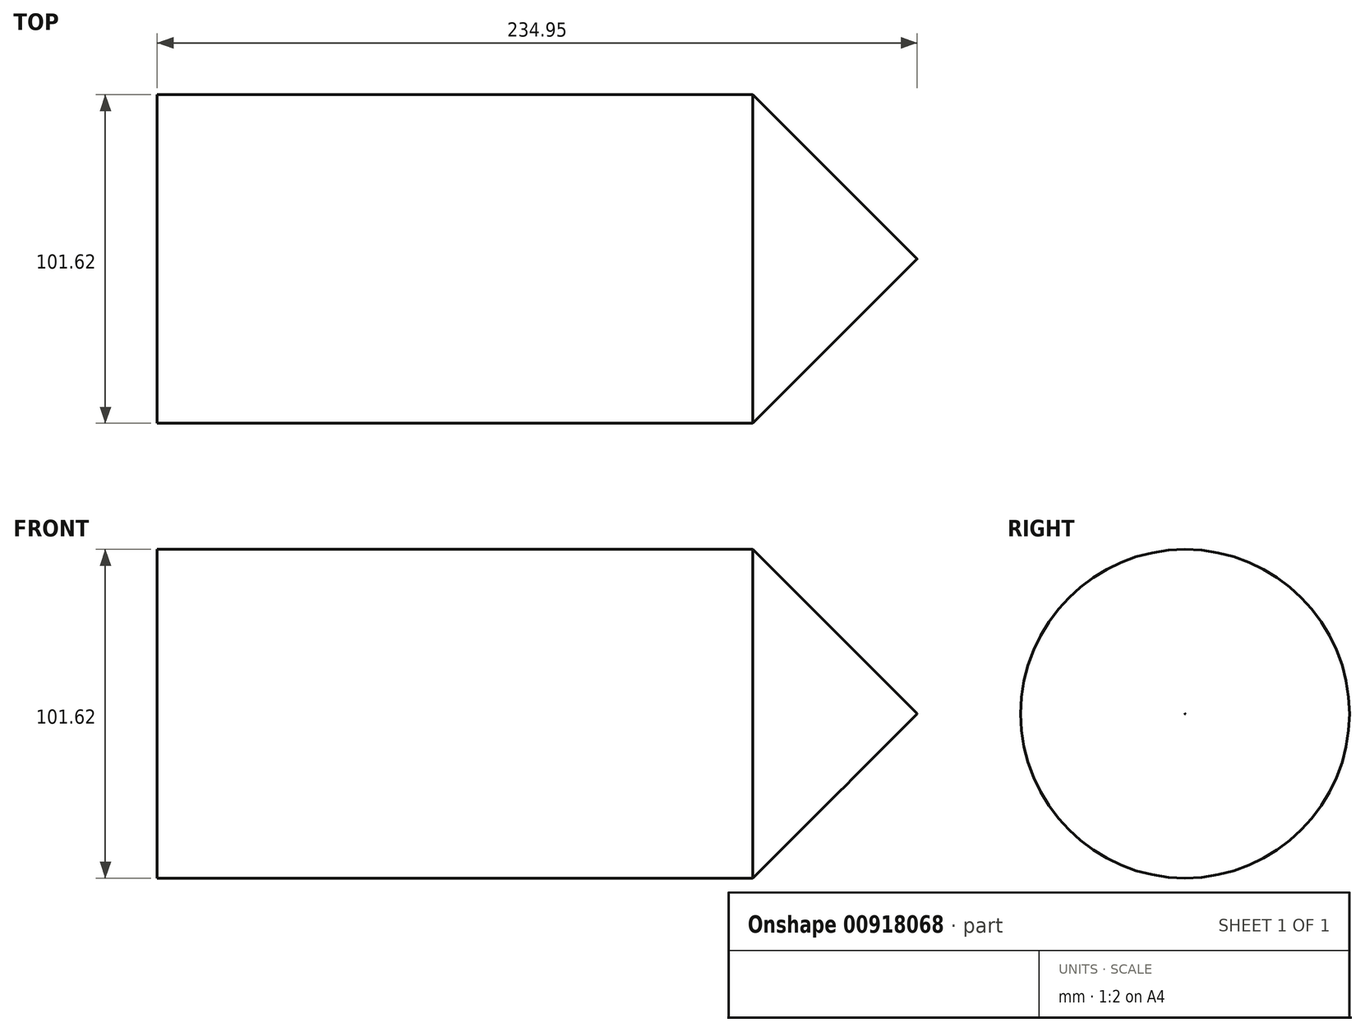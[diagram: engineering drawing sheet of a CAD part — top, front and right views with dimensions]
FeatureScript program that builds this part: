
annotation { "Feature Type Name" : "Feature", "Feature Type Description" : "" }
export const myFeature = defineFeature(function(context is Context, id is Id, definition is map)
    precondition{}
    {
        {
            var Q0;
            Q0=qCreatedBy(makeId("Right.planeOp"),FACE);
            var sketch = newSketch(context, id + "F0", { "sketchPlane" : qUnion([Q0])});
            skCircle(sketch, "E0", {"center": v(0, 0) * mm, "radius": 50.81 * mm});
            skSolve(sketch);
        }
        {
            var Q0;
            Q0=makeQuery(id+"F0.imprint","IMPRINT",FACE,{"disambiguationData":[TD([[makeQuery(id+"F0.imprint","IMPRINT",EDGE,{"derivedFrom":sQuery(id+"F0.wireOp",EDGE,"E0")}),1.0]])]});
            extrude(context, id + "F1", {"entities" : qUnion([Q0]), "depth" : 82.55 * mm, "offsetDistance" : 25.4 * mm});
        }
        {
            var Q0;
            Q0=makeQuery(id+"F1.opExtrude","CAP_EDGE",EDGE,{"disambiguationData":[OSD([sQuery(id+"F0.wireOp",EDGE,"E0")])],"isStart":false});
            chamfer(context, id + "F2", {"entities" : qUnion([Q0]), "width" : 50.8 * mm, "tangentPropagation" : true});
        }
        {
            var Q0;
            Q0=makeQuery(id+"F1.opExtrude","CAP_FACE",FACE,{"disambiguationData":[OSD([sQuery(id+"F0.wireOp",EDGE,"E0")])],"isStart":true});
            extrude(context, id + "F3", {"entities" : qUnion([Q0]), "operationType" : NewBodyOperationType.ADD, "depth" : 152.4 * mm, "offsetDistance" : 25.4 * mm});
        }
    });
